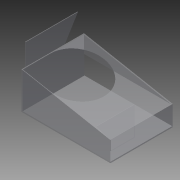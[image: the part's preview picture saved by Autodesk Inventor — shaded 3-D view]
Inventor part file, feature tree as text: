
AUTODESK INVENTOR PART (.ipt)
format: ipt  version: 2013 (Build 170138000, 138)  size: 202,752 bytes
history: native  units: in
note: dims shown in document units (in); Inventor stores cm internally (conversion verified against a paired STEP export)
features: extrude x11, sketch x11
ambient origin geometry x8: Origin, YZ Plane, XZ Plane, XY Plane, X Axis, Y Axis, Z Axis, Center Point
bodies: Solid1 (feature_tree)
feature tree (22):
  extrude  "Extrusion1"  Depth=0.125in TaperAngle=0.0deg
  extrude  "Extrusion2"  TaperAngle=90.0deg  [1 undecoded]
  extrude  "Extrusion3"  Depth=0.125in TaperAngle=0.0deg
  extrude  "Extrusion4"  Depth=13.0in
  extrude  "Extrusion5"  Depth=0.125in TaperAngle=0.0deg
  extrude  "Extrusion6"  Depth=0.125in TaperAngle=0.0deg
  extrude  "Extrusion7"  Depth=0.125in TaperAngle=0.0deg
  extrude  "Extrusion8"  Depth=11.5in
  extrude  "Extrusion9"  Depth=6.0in
  extrude  "Extrusion10"  Depth=5.0in
  extrude  "Extrusion11"  TaperAngle=0.0deg  [1 undecoded]
  sketch  "Sketch1"  dims[d0=3.5in d2=0.125in d3=0.0in]
  sketch  "Sketch2"  dims[d4=18.75in d5=90.0deg]
  sketch  "Sketch3"  dims[d6=13.0in d7=0.125in d8=0.0in]
  sketch  "Sketch4"  dims[d9=0.125in d10=13.0in]
  sketch  "Sketch5"  dims[d11=4.0in d12=0.125in d13=0.0in]
  sketch  "Sketch6"  dims[d14=13.0in d15=0.0in d16=0.125in d17=0.0in]
  sketch  "Sketch7"  dims[d18=13.0in d19=0.0in d20=0.125in d21=0.0in]
  sketch  "Sketch8"  dims[d22=0.125in d23=0.0in d24=11.5in]
  sketch  "Sketch9"  dims[d28=0.125in d29=0.0in d30=6.0in]
  sketch  "Sketch10"  dims[d31=8.0in d32=5.0in]
  sketch  "Sketch11"  dims[d33=2.0in d34=0.0in d35=0.0in d37=0.125in d38=0.0in d39=11.0in d40=6.5in d41=8.25in d42=2.0in d43=0.0in d44=0.875in d45=0.125in d46=0.0in d47=0.0in]
note: 2 required parameter values undecoded (feature->parameter linkage not recoverable at this tier; creation-order binding heuristic only, values carry confidence <= 0.55)
